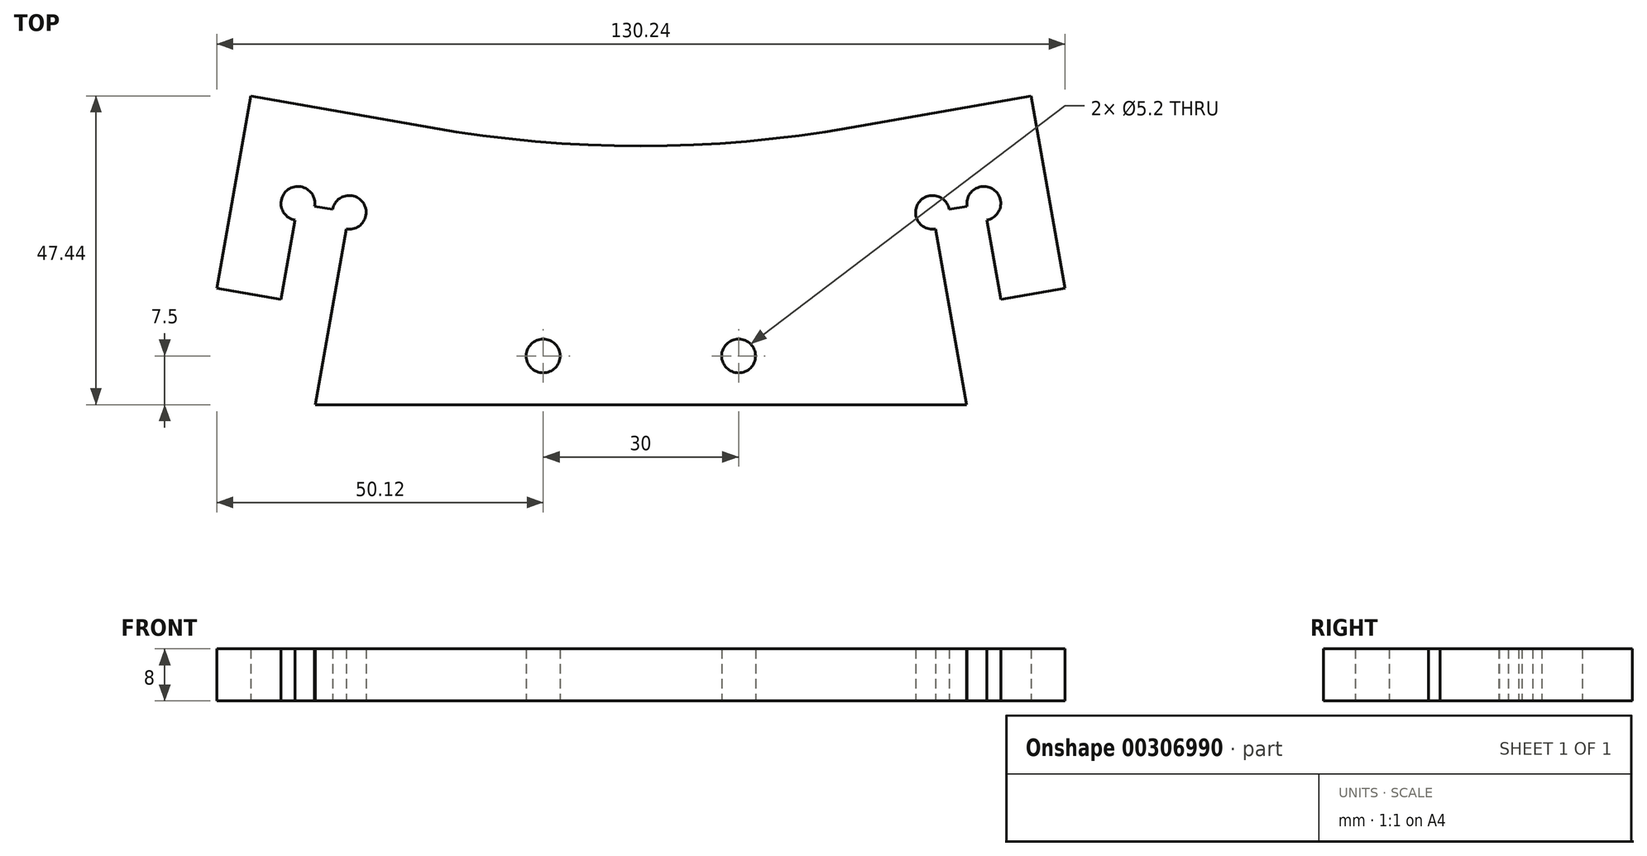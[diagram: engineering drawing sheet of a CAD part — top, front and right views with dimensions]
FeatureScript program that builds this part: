
annotation { "Feature Type Name" : "Feature", "Feature Type Description" : "" }
export const myFeature = defineFeature(function(context is Context, id is Id, definition is map)
    precondition{}
    {
        {
            var Q0;
            Q0=qCreatedBy(makeId("Top.planeOp"),FACE);
            var sketch = newSketch(context, id + "F0", { "sketchPlane" : qUnion([Q0])});
            skLineSegment(sketch, "E0.bottom", {"start": v(-47.36, 15) * mm, "end": v(47.36, 15) * mm});
            skLineSegment(sketch, "E0.top", {"start": v(-50, 0) * mm, "end": v(50, 0) * mm});
            skLineSegment(sketch, "E1", {"start": v(-50, 0) * mm, "end": v(-47.36, 15) * mm});
            skLineSegment(sketch, "E2", {"start": v(50, 0) * mm, "end": v(47.36, 15) * mm});
            skCircle(sketch, "E3", {"center": v(0, 7.5) * mm, "radius": 2.6 * mm});
            skLineSegment(sketch, "E4", {"start": v(0, 0) * mm, "end": v(0, 34.73) * mm, "construction": true});
            skCircle(sketch, "E5", {"center": v(-15, 7.5) * mm, "radius": 2.6 * mm});
            skCircle(sketch, "E6", {"center": v(15, 7.5) * mm, "radius": 2.6 * mm});
            skLineSegment(sketch, "E7", {"start": v(-47.36, 15) * mm, "end": v(-44.8, 29.54) * mm});
            skLineSegment(sketch, "E8", {"start": v(-44.8, 29.54) * mm, "end": v(-52.67, 30.93) * mm});
            skLineSegment(sketch, "E9", {"start": v(-52.67, 30.93) * mm, "end": v(-55.27, 16.16) * mm});
            skLineSegment(sketch, "E10", {"start": v(-55.27, 16.16) * mm, "end": v(-65.12, 17.9) * mm});
            skLineSegment(sketch, "E11", {"start": v(-65.12, 17.9) * mm, "end": v(-59.91, 47.44) * mm});
            skLineSegment(sketch, "E12", {"start": v(-59.91, 47.44) * mm, "end": v(-32.34, 42.58) * mm});
            skLineSegment(sketch, "E13", {"start": v(-32.34, 42.58) * mm, "end": v(-37.2, 15) * mm});
            skCircle(sketch, "E14", {"center": v(-52.67, 30.93) * mm, "radius": 2.6 * mm});
            skCircle(sketch, "E15", {"center": v(-44.8, 29.54) * mm, "radius": 2.6 * mm});
            skCircle(sketch, "E16.MirrorC", {"center": v(44.8, 29.54) * mm, "radius": 2.6 * mm});
            skLineSegment(sketch, "E17.MirrorCS", {"start": v(65.12, 17.9) * mm, "end": v(59.91, 47.44) * mm});
            skLineSegment(sketch, "E18.MirrorCS", {"start": v(55.27, 16.16) * mm, "end": v(65.12, 17.9) * mm});
            skLineSegment(sketch, "E19.MirrorCS", {"start": v(52.67, 30.93) * mm, "end": v(55.27, 16.16) * mm});
            skLineSegment(sketch, "E20.MirrorCS", {"start": v(44.8, 29.54) * mm, "end": v(52.67, 30.93) * mm});
            skLineSegment(sketch, "E21.MirrorCS", {"start": v(47.36, 15) * mm, "end": v(44.8, 29.54) * mm});
            skLineSegment(sketch, "E22.MirrorCS", {"start": v(59.91, 47.44) * mm, "end": v(32.34, 42.58) * mm});
            skLineSegment(sketch, "E23.MirrorCS", {"start": v(32.34, 42.58) * mm, "end": v(37.2, 15) * mm});
            skCircle(sketch, "E24.MirrorC", {"center": v(52.67, 30.93) * mm, "radius": 2.6 * mm});
            skArc(sketch, "E25", {"start": v(-32.34, 42.58) * mm, "mid": v(0, 39.75) * mm, "end": v(32.34, 42.58) * mm});
            skSolve(sketch);
        }
        {
            var Q0;
            Q0=makeQuery(id+"F0.imprint","IMPRINT",FACE,{"disambiguationData":[TD([[makeQuery(id+"F0.imprint","IMPRINT",EDGE,{"derivedFrom":sQuery(id+"F0.wireOp",EDGE,"E0.bottom")}),-1.0]])]});
            var Q1;
            Q1=makeQuery(id+"F0.imprint","IMPRINT",FACE,{"disambiguationData":[TD([[makeQuery(id+"F0.imprint","IMPRINT",EDGE,{"derivedFrom":sQuery(id+"F0.wireOp",EDGE,"E3")}),1.0]])]});
            var Q2;
            {var subQ0=sQuery(id+"F0.wireOp",EDGE,"E10");Q2=makeQuery(id+"F0.imprint","IMPRINT",FACE,{"disambiguationData":[TD([[makeQuery(id+"F0.imprint","IMPRINT",EDGE,{"derivedFrom":subQ0}),-1.0]])]});}
            var Q3;
            Q3=makeQuery(id+"F0.imprint","IMPRINT",FACE,{"disambiguationData":[TD([[makeQuery(id+"F0.imprint","IMPRINT",EDGE,{"derivedFrom":sQuery(id+"F0.wireOp",EDGE,"E17.MirrorCS")}),1.0]])]});
            var Q4;
            {var subQ0=sQuery(id+"F0.wireOp",EDGE,"E13");Q4=makeQuery(id+"F0.imprint","IMPRINT",FACE,{"disambiguationData":[TD([[makeQuery(id+"F0.imprint","IMPRINT",EDGE,{"derivedFrom":subQ0}),1.0]])]});}
            extrude(context, id + "F1", {"entities" : qUnion([Q0, Q1, Q2, Q3, Q4]), "depth" : 8 * mm});
        }
    });
